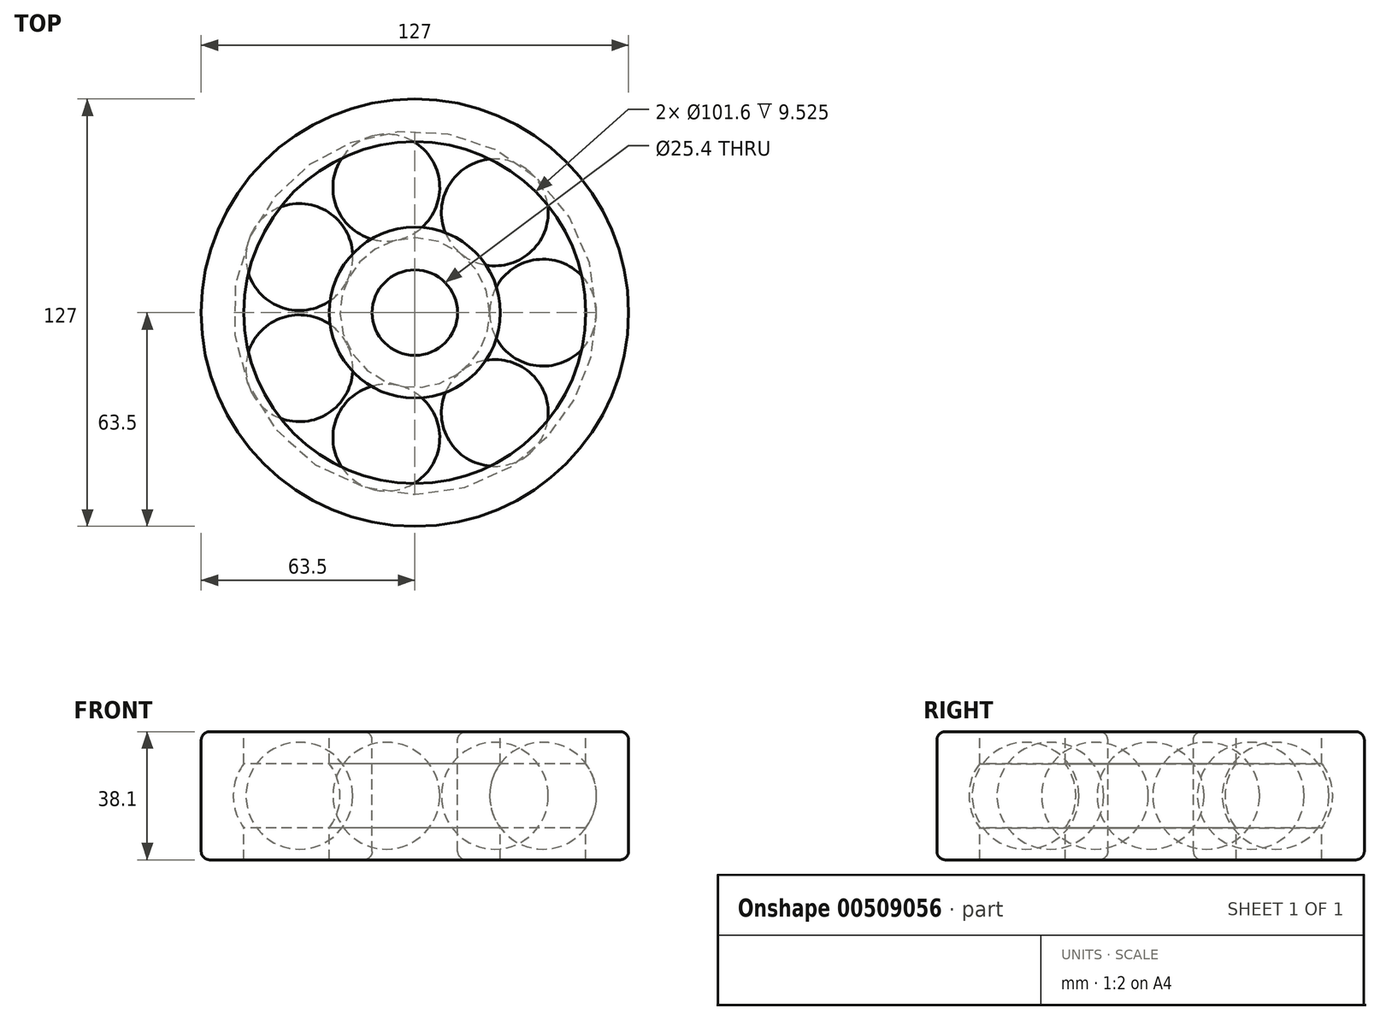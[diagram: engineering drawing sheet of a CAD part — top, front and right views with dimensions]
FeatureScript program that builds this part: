
annotation { "Feature Type Name" : "Feature", "Feature Type Description" : "" }
export const myFeature = defineFeature(function(context is Context, id is Id, definition is map)
    precondition{}
    {
        {
            var Q0;
            Q0=qCreatedBy(makeId("Front.planeOp"),FACE);
            var sketch = newSketch(context, id + "F0", { "sketchPlane" : qUnion([Q0])});
            skLineSegment(sketch, "E0", {"start": v(0, 19.05) * mm, "end": v(0, -19.05) * mm, "construction": true});
            skLineSegment(sketch, "E1", {"start": v(12.7, 19.05) * mm, "end": v(12.7, -19.05) * mm});
            skLineSegment(sketch, "E2", {"start": v(12.7, -19.05) * mm, "end": v(25.4, -19.05) * mm});
            skLineSegment(sketch, "E3", {"start": v(25.4, -19.05) * mm, "end": v(25.4, 19.05) * mm});
            skLineSegment(sketch, "E4", {"start": v(25.4, 19.05) * mm, "end": v(12.7, 19.05) * mm});
            skCircle(sketch, "E5", {"center": v(38.1, 0) * mm, "radius": 15.88 * mm});
            skLineSegment(sketch, "E6.bottom", {"start": v(50.8, 19.05) * mm, "end": v(63.5, 19.05) * mm});
            skLineSegment(sketch, "E6.top", {"start": v(50.8, -19.05) * mm, "end": v(63.5, -19.05) * mm});
            skLineSegment(sketch, "E6.left", {"start": v(50.8, 19.05) * mm, "end": v(50.8, -19.05) * mm});
            skLineSegment(sketch, "E6.right", {"start": v(63.5, 19.05) * mm, "end": v(63.5, -19.05) * mm});
            skLineSegment(sketch, "E7", {"start": v(22.22, 0) * mm, "end": v(53.97, 0) * mm});
            skLineSegment(sketch, "E8", {"start": v(12.7, 0) * mm, "end": v(22.22, 0) * mm, "construction": true});
            skLineSegment(sketch, "E9", {"start": v(53.97, 0) * mm, "end": v(63.5, 0) * mm, "construction": true});
            skSolve(sketch);
        }
        {
            var Q0;
            Q0=makeQuery(id+"F0.imprint","IMPRINT",FACE,{"disambiguationData":[TD([[makeQuery(id+"F0.imprint","IMPRINT",EDGE,{"derivedFrom":sQuery(id+"F0.wireOp",EDGE,"E1")}),1.0]])]});
            var Q1;
            {var subQ1=sQuery(id+"F0.wireOp",EDGE,"E6.bottom");Q1=makeQuery(id+"F0.imprint","IMPRINT",FACE,{"disambiguationData":[TD([[makeQuery(id+"F0.imprint","IMPRINT",EDGE,{"derivedFrom":subQ1}),-1.0]])]});}
            var Q2;
            Q2=sQuery(id+"F0.wireOp",EDGE,"E0");
            revolve(context, id + "F1", {"entities" : qUnion([Q0, Q1]), "axis" : qUnion([Q2]), "revolveType" : RevolveType.FULL});
        }
        {
            var Q0;
            {var subQ0=sQuery(id+"F0.wireOp",EDGE,"E5");var subQ1=sQuery(id+"F0.wireOp",EDGE,"E3");var subQ2=makeQuery(id+"F0.imprint","INTERSECT",VERTEX,{"disambiguationData":[OD(1.0)],"derivedFrom":[subQ1,subQ0]});Q0=makeQuery(id+"F0.imprint","IMPRINT",FACE,{"disambiguationData":[TD([[makeQuery(id+"F0.imprint","IMPRINT",EDGE,{"disambiguationData":[TD([[subQ2,1.0]])],"derivedFrom":subQ1}),1.0]])]});}
            var Q1;
            {var subQ0=sQuery(id+"F0.wireOp",EDGE,"E5");var subQ1=sQuery(id+"F0.wireOp",EDGE,"E3");var subQ2=makeQuery(id+"F0.imprint","INTERSECT",VERTEX,{"disambiguationData":[OD(1.0)],"derivedFrom":[subQ1,subQ0]});Q1=makeQuery(id+"F0.imprint","IMPRINT",FACE,{"disambiguationData":[TD([[makeQuery(id+"F0.imprint","IMPRINT",EDGE,{"disambiguationData":[TD([[subQ2,1.0]])],"derivedFrom":subQ1}),-1.0]])]});}
            var Q2;
            {var subQ0=sQuery(id+"F0.wireOp",EDGE,"E7");var subQ1=sQuery(id+"F0.wireOp",EDGE,"E5");var subQ2=makeQuery(id+"F0.imprint","INTERSECT",VERTEX,{"disambiguationData":[OD(1.0)],"derivedFrom":[subQ1,subQ0]});Q2=makeQuery(id+"F0.imprint","IMPRINT",FACE,{"disambiguationData":[TD([[makeQuery(id+"F0.imprint","IMPRINT",EDGE,{"disambiguationData":[TD([[subQ2,-1.0]])],"derivedFrom":subQ1}),1.0]])]});}
            var Q3;
            Q3=sQuery(id+"F0.wireOp",EDGE,"E7");
            revolve(context, id + "F2", {"entities" : qUnion([Q0, Q1, Q2]), "axis" : qUnion([Q3]), "revolveType" : RevolveType.FULL});
        }
        {
            var Q0;
            Q0=makeQuery(id+"F2.opRevolve","SWEPT_BODY",BODY,{"disambiguationData":[OSD([sQuery(id+"F0.wireOp",EDGE,"E5"),sQuery(id+"F0.wireOp",EDGE,"E7")])]});
            var Q1;
            Q1=sQuery(id+"F0.wireOp",EDGE,"E0");
            circularPattern(context, id + "F3", {"entities" : qUnion([Q0]), "axis" : qUnion([Q1]), "angle" : 360 * degree, "instanceCount" : 7, "equalSpace" : true, "computeTransformsWithoutBuiltin" : true});
        }
        {
            var Q0;
            Q0=makeQuery(id+"F1.opRevolve","SWEPT_EDGE",EDGE,{"disambiguationData":[OSD([sQuery(id+"F0.wireOp",EDGE,"E6.bottom"),sQuery(id+"F0.wireOp",EDGE,"E6.right")])]});
            var Q1;
            Q1=makeQuery(id+"F1.opRevolve","SWEPT_EDGE",EDGE,{"disambiguationData":[OSD([sQuery(id+"F0.wireOp",EDGE,"E6.top"),sQuery(id+"F0.wireOp",EDGE,"E6.right")])]});
            var Q2;
            Q2=makeQuery(id+"F1.opRevolve","SWEPT_EDGE",EDGE,{"disambiguationData":[OSD([sQuery(id+"F0.wireOp",EDGE,"E1"),sQuery(id+"F0.wireOp",EDGE,"E2")])]});
            var Q3;
            Q3=makeQuery(id+"F1.opRevolve","SWEPT_EDGE",EDGE,{"disambiguationData":[OSD([sQuery(id+"F0.wireOp",EDGE,"E1"),sQuery(id+"F0.wireOp",EDGE,"E4")])]});
            fillet(context, id + "F4", {"entities" : qUnion([Q0, Q1, Q2, Q3]), "radius" : 2.54 * mm, "tangentPropagation" : true, "allowEdgeOverflow" : false});
        }
    });
